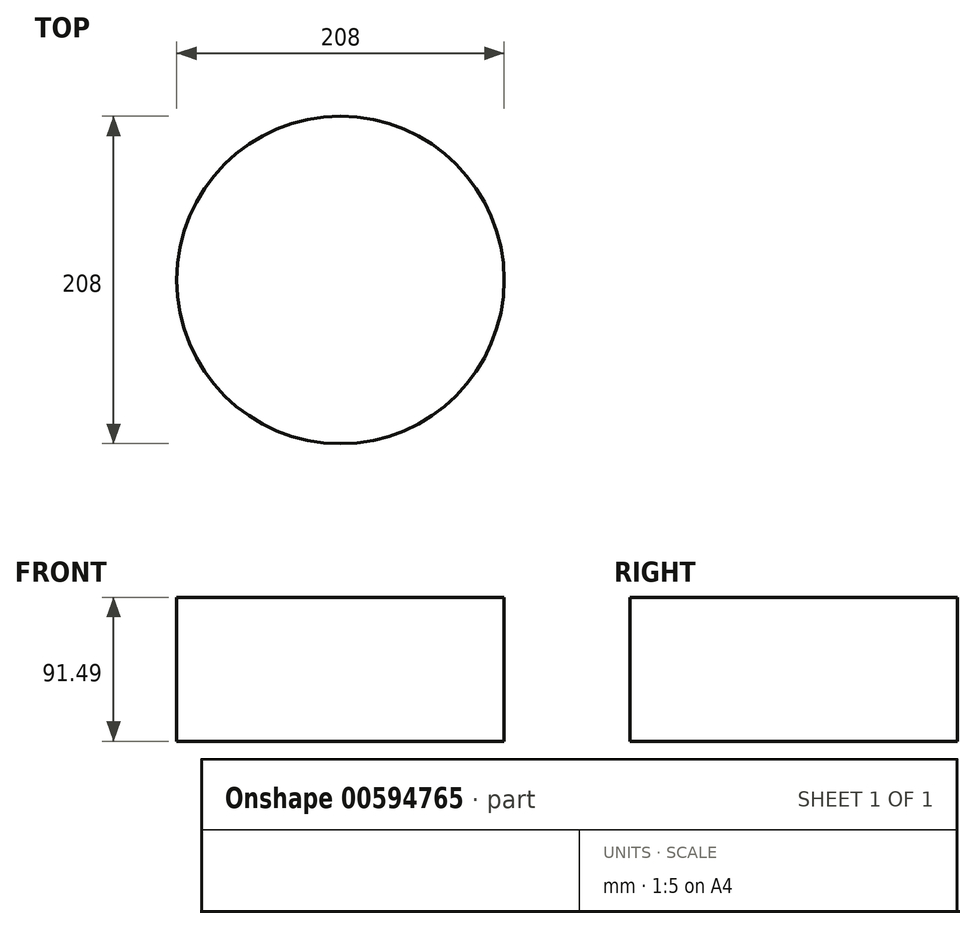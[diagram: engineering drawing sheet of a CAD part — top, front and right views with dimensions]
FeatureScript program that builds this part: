
annotation { "Feature Type Name" : "Feature", "Feature Type Description" : "" }
export const myFeature = defineFeature(function(context is Context, id is Id, definition is map)
    precondition{}
    {
        {
            var Q0;
            Q0=qCreatedBy(makeId("Front.planeOp"),FACE);
            var sketch = newSketch(context, id + "F0", { "sketchPlane" : qUnion([Q0])});
            skLineSegment(sketch, "E0.bottom", {"start": v(-51.12, 52.88) * mm, "end": v(52.88, 52.88) * mm});
            skLineSegment(sketch, "E0.top", {"start": v(-51.12, -38.6) * mm, "end": v(52.88, -38.6) * mm});
            skLineSegment(sketch, "E0.left", {"start": v(-51.12, 52.88) * mm, "end": v(-51.12, -38.6) * mm});
            skLineSegment(sketch, "E0.right", {"start": v(52.88, 52.88) * mm, "end": v(52.88, -38.6) * mm});
            skSolve(sketch);
        }
        {
            var Q0;
            Q0=makeQuery(id+"F0.imprint","IMPRINT",FACE,{"disambiguationData":[TD([[makeQuery(id+"F0.imprint","IMPRINT",EDGE,{"derivedFrom":sQuery(id+"F0.wireOp",EDGE,"E0.bottom")}),-1.0]])]});
            var Q1;
            Q1=sQuery(id+"F0.wireOp",EDGE,"E0.left");
            revolve(context, id + "F1", {"entities" : qUnion([Q0]), "axis" : qUnion([Q1]), "revolveType" : RevolveType.FULL});
        }
    });
